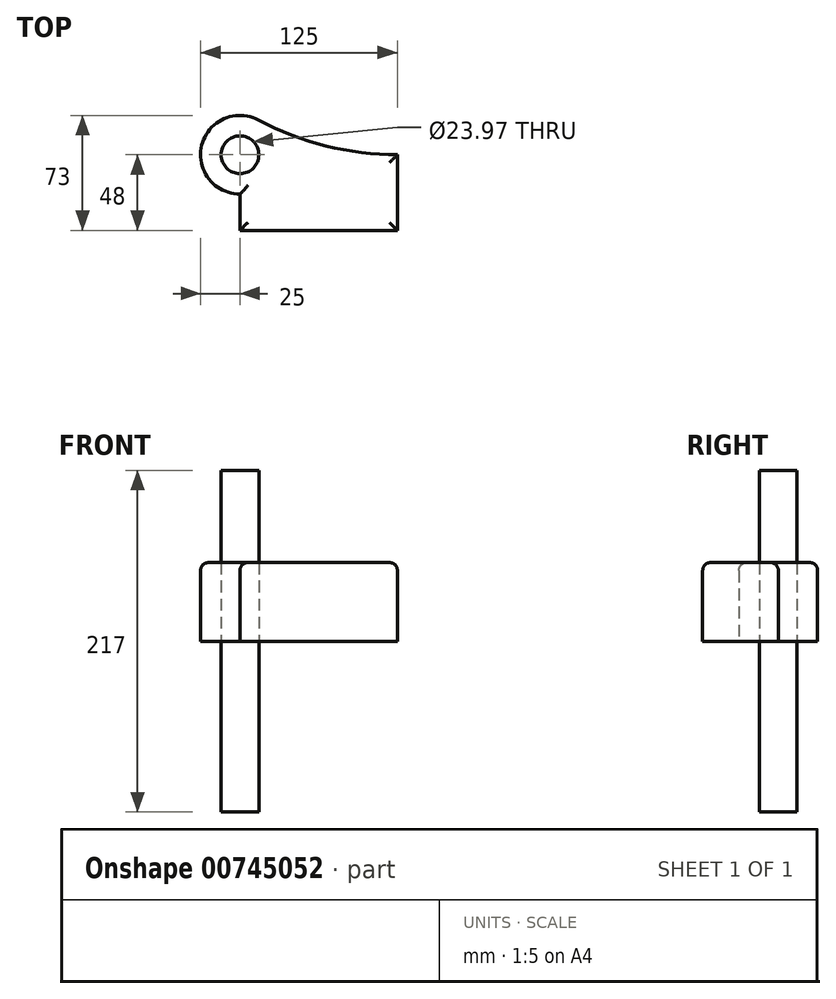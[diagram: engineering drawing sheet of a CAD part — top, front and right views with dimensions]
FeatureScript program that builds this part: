
annotation { "Feature Type Name" : "Feature", "Feature Type Description" : "" }
export const myFeature = defineFeature(function(context is Context, id is Id, definition is map)
    precondition{}
    {
        {
            var Q0;
            Q0=qCreatedBy(makeId("Top.planeOp"),FACE);
            var sketch = newSketch(context, id + "F0", { "sketchPlane" : qUnion([Q0])});
            skLineSegment(sketch, "E0.bottom", {"start": v(50, -24) * mm, "end": v(-50, -24) * mm});
            skLineSegment(sketch, "E0.top", {"start": v(50, 24) * mm, "end": v(-50, 24) * mm});
            skLineSegment(sketch, "E0.left", {"start": v(50, -24) * mm, "end": v(50, 24) * mm});
            skLineSegment(sketch, "E0.right", {"start": v(-50, -24) * mm, "end": v(-50, 24) * mm});
            skPoint(sketch, "E0.middle", {"position": v(0, 0) * mm});
            skCircle(sketch, "E1", {"center": v(-50, 24) * mm, "radius": 25 * mm});
            skArc(sketch, "E2", {"start": v(-38.24, 46.06) * mm, "mid": v(4.52, 29.6) * mm, "end": v(50, 24) * mm});
            skCircle(sketch, "E3", {"center": v(-50, 24) * mm, "radius": 11.99 * mm});
            skSolve(sketch);
        }
        {
            var Q0;
            {var subQ0=sQuery(id+"F0.wireOp",EDGE,"E1");var subQ4=sQuery(id+"F0.wireOp",EDGE,"E0.top");var subQ5=makeQuery(id+"F0.imprint","INTERSECT",VERTEX,{"derivedFrom":[subQ4,subQ0]});Q0=makeQuery(id+"F0.imprint","IMPRINT",FACE,{"disambiguationData":[TD([[makeQuery(id+"F0.imprint","IMPRINT",EDGE,{"disambiguationData":[TD([[subQ5,-1.0]])],"derivedFrom":subQ4}),-1.0]])]});}
            var Q1;
            {var subQ0=sQuery(id+"F0.wireOp",EDGE,"E1");var subQ1=sQuery(id+"F0.wireOp",EDGE,"E0.top");var subQ2=makeQuery(id+"F0.imprint","INTERSECT",VERTEX,{"derivedFrom":[subQ1,subQ0]});Q1=makeQuery(id+"F0.imprint","IMPRINT",FACE,{"disambiguationData":[TD([[makeQuery(id+"F0.imprint","IMPRINT",EDGE,{"disambiguationData":[TD([[subQ2,-1.0]])],"derivedFrom":subQ1}),1.0]])]});}
            var Q2;
            {var subQ5=sQuery(id+"F0.wireOp",EDGE,"E0.bottom");Q2=makeQuery(id+"F0.imprint","IMPRINT",FACE,{"disambiguationData":[TD([[makeQuery(id+"F0.imprint","IMPRINT",EDGE,{"derivedFrom":subQ5}),-1.0]])]});}
            var Q3;
            {var subQ0=sQuery(id+"F0.wireOp",EDGE,"E2");Q3=makeQuery(id+"F0.imprint","IMPRINT",FACE,{"disambiguationData":[TD([[makeQuery(id+"F0.imprint","IMPRINT",EDGE,{"derivedFrom":subQ0}),-1.0]])]});}
            extrude(context, id + "F1", {"entities" : qUnion([Q0, Q1, Q2, Q3]), "depth" : 50 * mm, "offsetDistance" : 25 * mm});
        }
        {
            var Q0;
            {var subQ0=sQuery(id+"F0.wireOp",EDGE,"E0.right");var subQ1=sQuery(id+"F0.wireOp",EDGE,"E0.top");var subQ2=makeQuery(id+"F0.imprint","INTERSECT",VERTEX,{"derivedFrom":[subQ1,subQ0]});Q0=makeQuery(id+"F0.imprint","IMPRINT",FACE,{"disambiguationData":[TD([[makeQuery(id+"F0.imprint","IMPRINT",EDGE,{"disambiguationData":[TD([[subQ2,1.0]])],"derivedFrom":subQ1}),1.0]])]});}
            var Q1;
            {var subQ0=sQuery(id+"F0.wireOp",EDGE,"E0.right");var subQ1=sQuery(id+"F0.wireOp",EDGE,"E0.top");var subQ2=makeQuery(id+"F0.imprint","INTERSECT",VERTEX,{"derivedFrom":[subQ1,subQ0]});Q1=makeQuery(id+"F0.imprint","IMPRINT",FACE,{"disambiguationData":[TD([[makeQuery(id+"F0.imprint","IMPRINT",EDGE,{"disambiguationData":[TD([[subQ2,1.0]])],"derivedFrom":subQ1}),-1.0]])]});}
            extrude(context, id + "F2", {"entities" : qUnion([Q0, Q1]), "endBound" : BoundingType.SYMMETRIC, "depth" : 217 * mm, "offsetDistance" : 25 * mm});
        }
        {
            var Q0;
            Q0=makeQuery(id+"F1.opExtrude","CAP_EDGE",EDGE,{"disambiguationData":[OSD([sQuery(id+"F0.wireOp",EDGE,"E1")])],"isStart":false});
            var Q1;
            Q1=makeQuery(id+"F1.opExtrude","CAP_EDGE",EDGE,{"disambiguationData":[OSD([sQuery(id+"F0.wireOp",EDGE,"E0.right")])],"isStart":false});
            var Q2;
            Q2=makeQuery(id+"F1.opExtrude","CAP_EDGE",EDGE,{"disambiguationData":[OSD([sQuery(id+"F0.wireOp",EDGE,"E0.bottom")])],"isStart":false});
            var Q3;
            Q3=makeQuery(id+"F1.opExtrude","CAP_EDGE",EDGE,{"disambiguationData":[OSD([sQuery(id+"F0.wireOp",EDGE,"E0.left")])],"isStart":false});
            fillet(context, id + "F3", {"entities" : qUnion([Q0, Q1, Q2, Q3]), "radius" : 5 * mm, "tangentPropagation" : true, "allowEdgeOverflow" : false});
        }
    });
